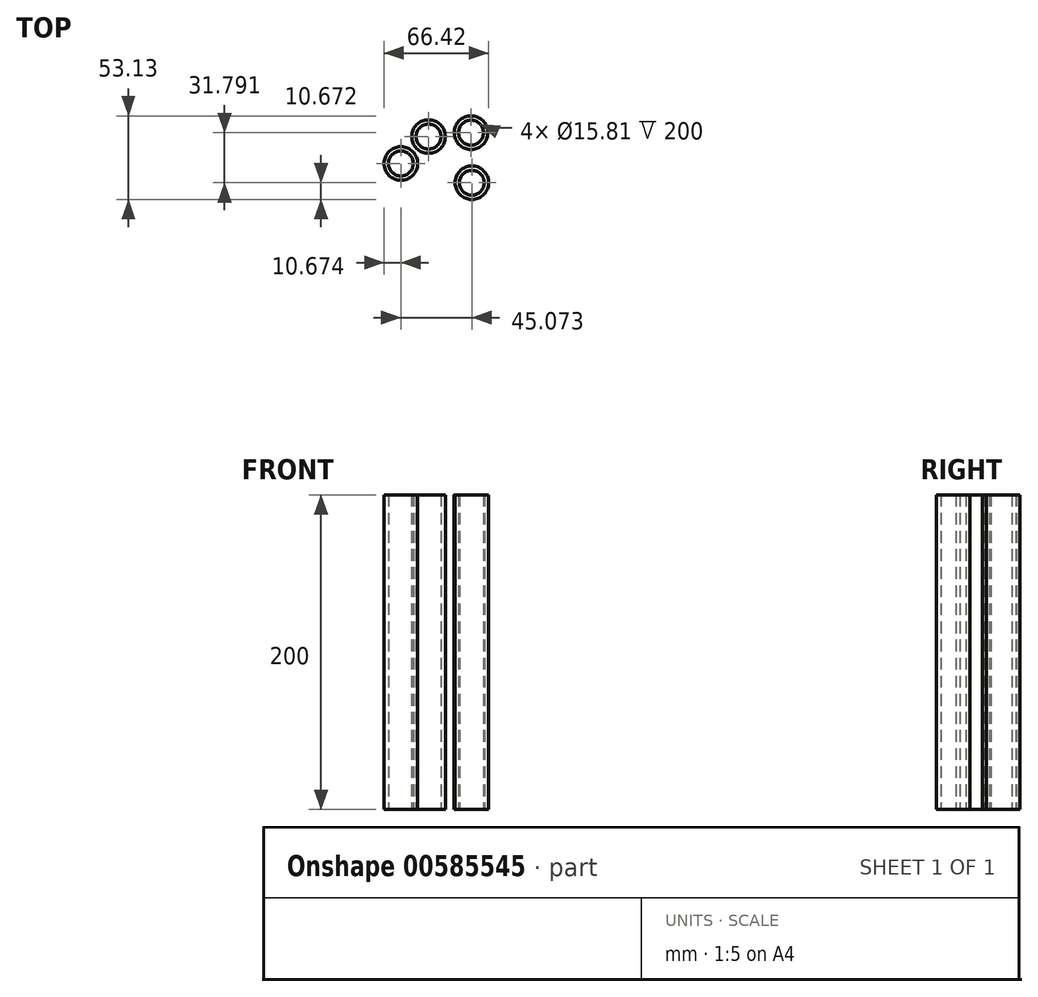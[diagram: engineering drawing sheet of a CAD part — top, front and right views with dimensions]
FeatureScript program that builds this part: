
annotation { "Feature Type Name" : "Feature", "Feature Type Description" : "" }
export const myFeature = defineFeature(function(context is Context, id is Id, definition is map)
    precondition{}
    {
        {
            var Q0;
            Q0=qCreatedBy(makeId("Top.planeOp"),FACE);
            var sketch = newSketch(context, id + "F0", { "sketchPlane" : qUnion([Q0])});
            skCircle(sketch, "E0", {"center": v(19.36, 17.27) * mm, "radius": 10.67 * mm});
            skCircle(sketch, "E1", {"center": v(19.36, 17.27) * mm, "radius": 7.9 * mm});
            skSolve(sketch);
        }
        {
            var Q0;
            Q0=makeQuery(id+"F0.imprint","IMPRINT",FACE,{"disambiguationData":[TD([[makeQuery(id+"F0.imprint","IMPRINT",EDGE,{"derivedFrom":sQuery(id+"F0.wireOp",EDGE,"E0")}),1.0]])]});
            extrude(context, id + "F1", {"entities" : qUnion([Q0]), "depth" : 200 * mm, "offsetDistance" : 25.4 * mm});
        }
        {
            var Q0;
            Q0=qCreatedBy(makeId("Top.planeOp"),FACE);
            var sketch = newSketch(context, id + "F2", { "sketchPlane" : qUnion([Q0])});
            skCircle(sketch, "E2", {"center": v(19.86, -14.52) * mm, "radius": 10.67 * mm});
            skCircle(sketch, "E3", {"center": v(19.86, -14.52) * mm, "radius": 7.9 * mm});
            skCircle(sketch, "E4", {"center": v(-25.22, -2.28) * mm, "radius": 10.67 * mm});
            skCircle(sketch, "E5", {"center": v(-25.22, -2.28) * mm, "radius": 7.9 * mm});
            skCircle(sketch, "E6", {"center": v(-7.64, 14.8) * mm, "radius": 10.67 * mm});
            skCircle(sketch, "E7", {"center": v(-7.64, 14.8) * mm, "radius": 7.9 * mm});
            skSolve(sketch);
        }
        {
            var Q0;
            Q0=makeQuery(id+"F2.imprint","IMPRINT",FACE,{"disambiguationData":[TD([[makeQuery(id+"F2.imprint","IMPRINT",EDGE,{"derivedFrom":sQuery(id+"F2.wireOp",EDGE,"E2")}),1.0]])]});
            extrude(context, id + "F3", {"entities" : qUnion([Q0]), "depth" : 200 * mm, "offsetDistance" : 25 * mm});
        }
        {
            var Q0;
            Q0=makeQuery(id+"F2.imprint","IMPRINT",FACE,{"disambiguationData":[TD([[makeQuery(id+"F2.imprint","IMPRINT",EDGE,{"derivedFrom":sQuery(id+"F2.wireOp",EDGE,"E4")}),1.0]])]});
            extrude(context, id + "F4", {"entities" : qUnion([Q0]), "depth" : 200 * mm, "offsetDistance" : 25 * mm});
        }
        {
            var Q0;
            Q0=makeQuery(id+"F2.imprint","IMPRINT",FACE,{"disambiguationData":[TD([[makeQuery(id+"F2.imprint","IMPRINT",EDGE,{"derivedFrom":sQuery(id+"F2.wireOp",EDGE,"E6")}),1.0]])]});
            extrude(context, id + "F5", {"entities" : qUnion([Q0]), "depth" : 200 * mm, "offsetDistance" : 25 * mm});
        }
    });
